# Revit family: CADS_AIRFLOWdev_AirRound_OffsetReducer
name_source: partatom
category: Duct Fittings
revit_build: Autodesk Revit 2015 (Build: 20160512_1515(x64)
units: mm (PartAtom-declared; Revit-internal decimal feet)

## types (1)
- CADS_AIRFLOWdev_AirRound_OffsetReducer
    6MonthlyMaintenance = Visually inspect system, clean the fan and ducting if necessary
    AirflowRateRange = 140.0 L/s
    AssemblyPlace = UNKNOWN
    AssetType = FIXED
    Body = CADS_AirFlow_White
    CADS_Index = 0
    CEApproval = Yes
    Color = White
    Constituents = 125mm to 100mm offset reducer (for rigid pipe)
    DurationUnit = Year
    ExpectedServiceLife = 10
    Features = 125mm to 100mm offset reducer (for rigid pipe)
    Finish = Lacquer
    FireControlPanelLinks = No
    Fitting Type = Ignore
    Grade = Virgin
    GrossWeight = 0.05 kg
    ISO140001 = Yes
    ISO90001 = Yes
    IsExtendedWarranty = No
    LongitudinalSeam = None
    Manufacturer = Airflow Developments Ltd
    ManufacturerAddress = Aidelle House
Lancaster Road
Cressex Business Park
High Wycombe
Bucks
HP123QP
    ManufacturerTelephone = 01494 525252
    ManufacturerWebsite = www.airflow.com
    Material = Plastic
    NBSCode = 45-80-50/394 Ventilation ducts
    NominalHeight = 125 mm  [stored 0.410105 ft]
    NominalLength = 75 mm
    NominalWidth = 125 mm  [stored 0.410105 ft]
    PassiveHouseApproval = No
    PointOfContact = Airflow Developments Ltd
    ProductLiterature = https://www.airflow.com
    ProductionYear = 2017
    Quantity = 1
    RedDotDesignAward = No
    ReplacementCost = 2.568
    SAPApproval = No
    ServiceLifeDuration = 10
    ServiceLifeType = EXPECTEDSERVICELIFE
    Shape = Round
    ShippingWeight = 0.06 kg
    Size = 75 x 125 x 125
    Status = New
    TemperatureRange = up to 40°C
    Uniclass2015 = Pr_30_59_96_92:Ventilation ducts
    WarrantyGuarantor = Airflow Developments Ltd
    WarrantyPeriod = 0
    WorkingPressure = 3000.0 Pa

note: [stored X ft] marks values corroborated as IEEE doubles in the binary element streams (Revit-internal decimal feet)

## geometry (parser evidence)
native form markers: Blend x2, Sweep x3
no freeform markers — native parametric forms only
